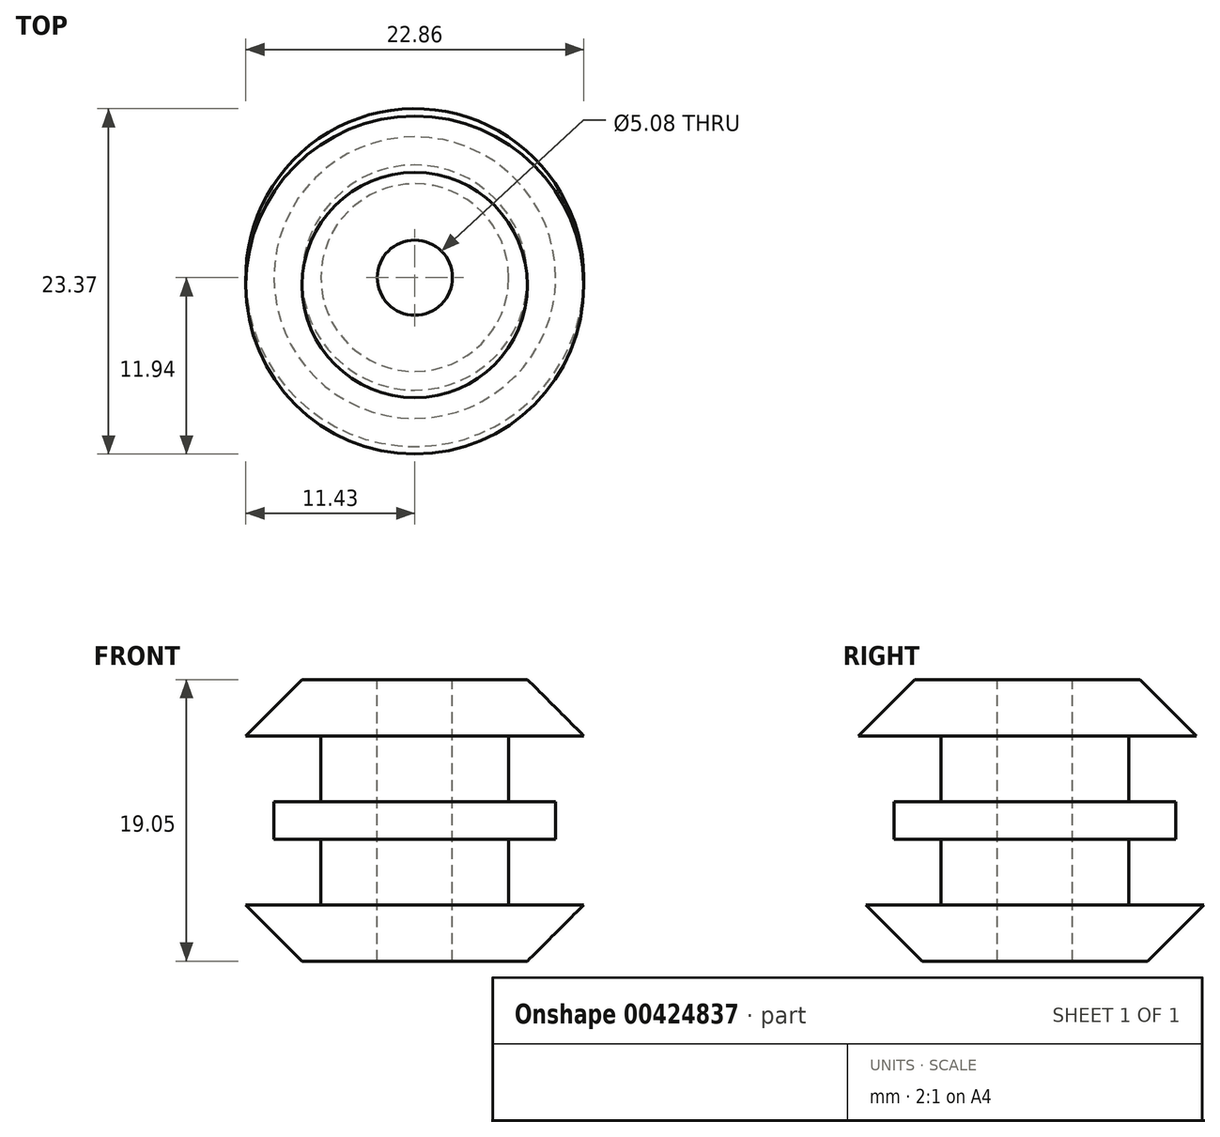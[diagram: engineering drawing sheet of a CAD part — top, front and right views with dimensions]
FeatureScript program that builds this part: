
annotation { "Feature Type Name" : "Feature", "Feature Type Description" : "" }
export const myFeature = defineFeature(function(context is Context, id is Id, definition is map)
    precondition{}
    {
        {
            var Q0;
            Q0=qCreatedBy(makeId("Top.planeOp"),FACE);
            var sketch = newSketch(context, id + "F0", { "sketchPlane" : qUnion([Q0])});
            skCircle(sketch, "E0", {"center": v(0, 0) * mm, "radius": 12.7 * mm});
            skSolve(sketch);
        }
        {
            var Q0;
            Q0 = qSketchRegion(id + "F0", true);
            extrude(context, id + "F1", {"entities" : qUnion([Q0]), "depth" : 3.8 * mm});
        }
        {
            var Q0;
            Q0=makeQuery(id+"F1.opExtrude","CAP_FACE",FACE,{"disambiguationData":[OSD([sQuery(id+"F0.wireOp",EDGE,"E0")])],"isStart":false});
            var sketch = newSketch(context, id + "F2", { "sketchPlane" : qUnion([Q0])});
            skCircle(sketch, "E1", {"center": v(0, 0) * mm, "radius": 6.35 * mm});
            skSolve(sketch);
        }
        {
            var Q0;
            Q0 = qSketchRegion(id + "F2", true);
            extrude(context, id + "F3", {"entities" : qUnion([Q0]), "operationType" : NewBodyOperationType.ADD, "depth" : 4.44 * mm});
        }
        {
            var Q0;
            Q0=makeQuery(id+"F3.opExtrude","CAP_FACE",FACE,{"disambiguationData":[OSD([sQuery(id+"F2.wireOp",EDGE,"E1")])],"isStart":false});
            var sketch = newSketch(context, id + "F4", { "sketchPlane" : qUnion([Q0])});
            skCircle(sketch, "E2", {"center": v(0, 0) * mm, "radius": 9.53 * mm});
            skSolve(sketch);
        }
        {
            var Q0;
            Q0 = qSketchRegion(id + "F4", true);
            extrude(context, id + "F5", {"entities" : qUnion([Q0]), "operationType" : NewBodyOperationType.ADD, "depth" : 2.54 * mm});
        }
        {
            var Q0;
            Q0=makeQuery(id+"F5.opExtrude","CAP_FACE",FACE,{"disambiguationData":[OSD([sQuery(id+"F4.wireOp",EDGE,"E2")])],"isStart":false});
            var sketch = newSketch(context, id + "F6", { "sketchPlane" : qUnion([Q0])});
            skCircle(sketch, "E3", {"center": v(0, 0) * mm, "radius": 6.35 * mm});
            skSolve(sketch);
        }
        {
            var Q0;
            Q0 = qSketchRegion(id + "F6", true);
            extrude(context, id + "F7", {"entities" : qUnion([Q0]), "operationType" : NewBodyOperationType.ADD, "depth" : 4.44 * mm});
        }
        {
            var Q0;
            Q0=makeQuery(id+"F7.opExtrude","CAP_FACE",FACE,{"disambiguationData":[OSD([sQuery(id+"F6.wireOp",EDGE,"E3")])],"isStart":false});
            var sketch = newSketch(context, id + "F8", { "sketchPlane" : qUnion([Q0])});
            skCircle(sketch, "E4", {"center": v(0, -0.5) * mm, "radius": 12.7 * mm});
            skSolve(sketch);
        }
        {
            var Q0;
            Q0 = qSketchRegion(id + "F8", true);
            extrude(context, id + "F9", {"entities" : qUnion([Q0]), "operationType" : NewBodyOperationType.ADD, "depth" : 3.8 * mm});
        }
        {
            var Q0;
            Q0=makeQuery(id+"F9.opExtrude","CAP_FACE",FACE,{"disambiguationData":[OSD([sQuery(id+"F8.wireOp",EDGE,"E4")])],"isStart":false});
            var sketch = newSketch(context, id + "F10", { "sketchPlane" : qUnion([Q0])});
            skCircle(sketch, "E5", {"center": v(0, 0) * mm, "radius": 2.54 * mm});
            skSolve(sketch);
        }
        {
            var Q0;
            Q0 = qSketchRegion(id + "F10", true);
            extrude(context, id + "F11", {"entities" : qUnion([Q0]), "operationType" : NewBodyOperationType.REMOVE, "oppositeDirection" : true, "depth" : 19.05 * mm});
        }
        {
            var Q0;
            Q0=makeQuery(id+"F9.opExtrude","CAP_EDGE",EDGE,{"disambiguationData":[OSD([sQuery(id+"F8.wireOp",EDGE,"E4")])],"isStart":false});
            chamfer(context, id + "F12", {"entities" : qUnion([Q0]), "width" : 5.08 * mm, "tangentPropagation" : true});
        }
        {
            var Q0;
            Q0=makeQuery(id+"F1.opExtrude","CAP_EDGE",EDGE,{"disambiguationData":[OSD([sQuery(id+"F0.wireOp",EDGE,"E0")])],"isStart":true});
            chamfer(context, id + "F13", {"entities" : qUnion([Q0]), "width" : 5.08 * mm, "tangentPropagation" : true});
        }
    });
